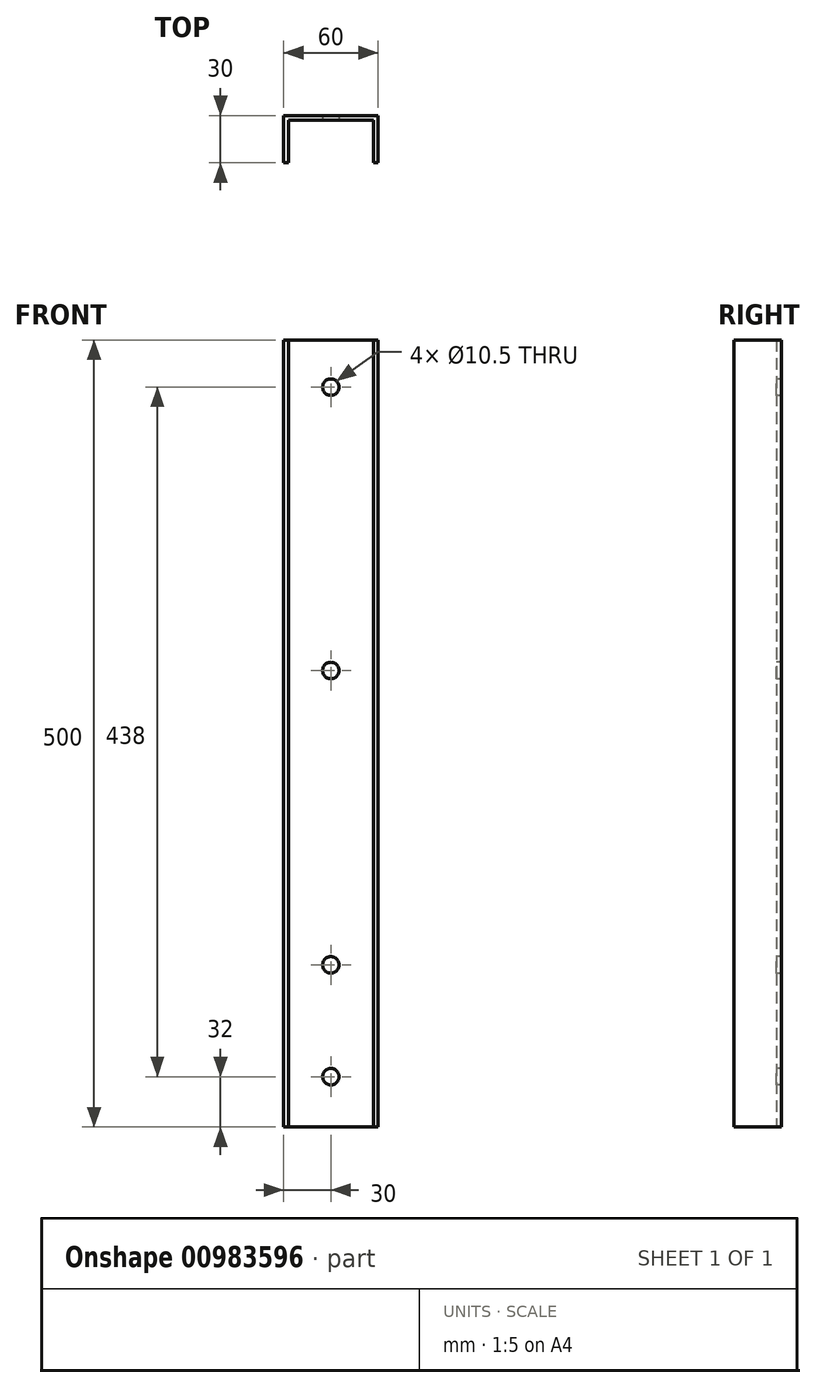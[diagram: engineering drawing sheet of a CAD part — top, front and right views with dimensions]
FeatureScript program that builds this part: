
annotation { "Feature Type Name" : "Feature", "Feature Type Description" : "" }
export const myFeature = defineFeature(function(context is Context, id is Id, definition is map)
    precondition{}
    {
        {
            var Q0;
            Q0=qCreatedBy(makeId("Top.planeOp"),FACE);
            var sketch = newSketch(context, id + "F0", { "sketchPlane" : qUnion([Q0])});
            skLineSegment(sketch, "E0.bottom", {"start": v(30, -15) * mm, "end": v(-30, -15) * mm, "construction": true});
            skLineSegment(sketch, "E0.top", {"start": v(30, 15) * mm, "end": v(-30, 15) * mm, "construction": true});
            skLineSegment(sketch, "E0.left", {"start": v(30, -15) * mm, "end": v(30, 15) * mm, "construction": true});
            skLineSegment(sketch, "E0.right", {"start": v(-30, -15) * mm, "end": v(-30, 15) * mm, "construction": true});
            skPoint(sketch, "E0.middle", {"position": v(0, 0) * mm});
            skLineSegment(sketch, "E1", {"start": v(-30, 15) * mm, "end": v(30, 15) * mm});
            skLineSegment(sketch, "E2", {"start": v(30, -15) * mm, "end": v(27, -15) * mm});
            skLineSegment(sketch, "E3", {"start": v(27, -15) * mm, "end": v(27, 12) * mm});
            skLineSegment(sketch, "E4", {"start": v(27, 12) * mm, "end": v(-27, 12) * mm});
            skLineSegment(sketch, "E5", {"start": v(-27, 12) * mm, "end": v(-27, -15) * mm});
            skLineSegment(sketch, "E6", {"start": v(-27, -15) * mm, "end": v(-30, -15) * mm});
            skLineSegment(sketch, "E7", {"start": v(-30, -15) * mm, "end": v(-30, 15) * mm});
            skLineSegment(sketch, "E8", {"start": v(30, -15) * mm, "end": v(30, 15) * mm});
            skSolve(sketch);
        }
        {
            var Q0;
            Q0=makeQuery(id+"F0.imprint","IMPRINT",FACE,{"disambiguationData":[TD([[makeQuery(id+"F0.imprint","IMPRINT",EDGE,{"derivedFrom":sQuery(id+"F0.wireOp",EDGE,"E1")}),-1.0]])]});
            extrude(context, id + "F1", {"entities" : qUnion([Q0]), "depth" : 500 * mm, "offsetDistance" : 25 * mm, "symmetric" : true});
        }
        {
            var Q0;
            Q0=makeQuery(id+"F1.opExtrude","SWEPT_FACE",FACE,{"disambiguationData":[OSD([sQuery(id+"F0.wireOp",EDGE,"E1")])]});
            var sketch = newSketch(context, id + "F2", { "sketchPlane" : qUnion([Q0])});
            skLineSegment(sketch, "E9", {"start": v(0, -250) * mm, "end": v(0, 250) * mm, "construction": true});
            skPoint(sketch, "E10", {"position": v(0, -218) * mm});
            skPoint(sketch, "E11", {"position": v(0, -147) * mm});
            skPoint(sketch, "E12", {"position": v(0, 220) * mm});
            skPoint(sketch, "E13", {"position": v(0, 40) * mm});
            skSolve(sketch);
        }
        {
            var Q0;
            Q0=sQuery(id+"F2.wireOp",VERTEX,"E10");
            var Q1;
            Q1=sQuery(id+"F2.wireOp",VERTEX,"E11");
            var Q2;
            Q2=makeQuery(id+"F1.opExtrude","SWEPT_BODY",BODY,{"disambiguationData":[OSD([sQuery(id+"F0.wireOp",EDGE,"E1"),sQuery(id+"F0.wireOp",EDGE,"E2"),sQuery(id+"F0.wireOp",EDGE,"E3"),sQuery(id+"F0.wireOp",EDGE,"E4"),sQuery(id+"F0.wireOp",EDGE,"E5"),sQuery(id+"F0.wireOp",EDGE,"E6"),sQuery(id+"F0.wireOp",EDGE,"E7"),sQuery(id+"F0.wireOp",EDGE,"E8")])]});
            hole(context, id + "F3", {"style" : HoleStyle.SIMPLE, "endStyle" : HoleEndStyle.THROUGH, "standardTappedOrClearance" : lookupTablePath({ "standard" : "ISO", "size" : "10.5", "type" : "Drilled" }), "standardBlindInLast" : lookupTablePath({ "standard" : "ISO", "size" : "10.5", "type" : "Drilled" }), "holeDiameter" : 10.5 * mm, "majorDiameter" : 5 * mm, "isTappedThrough" : true, "tappedDepth" : 19 * mm, "tapClearance" : 3, "startFromSketch" : true, "locations" : qUnion([Q0, Q1]), "scope" : qUnion([Q2])});
        }
        {
            var Q0;
            Q0=makeQuery(id+"F1.opExtrude","SWEPT_FACE",FACE,{"disambiguationData":[OSD([sQuery(id+"F0.wireOp",EDGE,"E1")])]});
            var sketch = newSketch(context, id + "F4", { "sketchPlane" : qUnion([Q0])});
            skLineSegment(sketch, "E14", {"start": v(0, 250) * mm, "end": v(0, -250) * mm, "construction": true});
            skPoint(sketch, "E15", {"position": v(0, 220) * mm});
            skPoint(sketch, "E16", {"position": v(0, 40) * mm});
            skSolve(sketch);
        }
        {
            var Q0;
            Q0=sQuery(id+"F4.wireOp",VERTEX,"E15");
            var Q1;
            Q1=sQuery(id+"F4.wireOp",VERTEX,"E16");
            var Q2;
            Q2=makeQuery(id+"F1.opExtrude","SWEPT_BODY",BODY,{"disambiguationData":[OSD([sQuery(id+"F0.wireOp",EDGE,"E1"),sQuery(id+"F0.wireOp",EDGE,"E2"),sQuery(id+"F0.wireOp",EDGE,"E3"),sQuery(id+"F0.wireOp",EDGE,"E4"),sQuery(id+"F0.wireOp",EDGE,"E5"),sQuery(id+"F0.wireOp",EDGE,"E6"),sQuery(id+"F0.wireOp",EDGE,"E7"),sQuery(id+"F0.wireOp",EDGE,"E8")])]});
            hole(context, id + "F5", {"style" : HoleStyle.SIMPLE, "endStyle" : HoleEndStyle.THROUGH, "standardTappedOrClearance" : lookupTablePath({ "standard" : "ISO", "size" : "10.5", "type" : "Drilled" }), "standardBlindInLast" : lookupTablePath({ "standard" : "ISO", "size" : "10.5", "type" : "Drilled" }), "holeDiameter" : 10.5 * mm, "majorDiameter" : 5 * mm, "isTappedThrough" : true, "tappedDepth" : 19 * mm, "tapClearance" : 3, "startFromSketch" : true, "locations" : qUnion([Q0, Q1]), "scope" : qUnion([Q2])});
        }
    });
